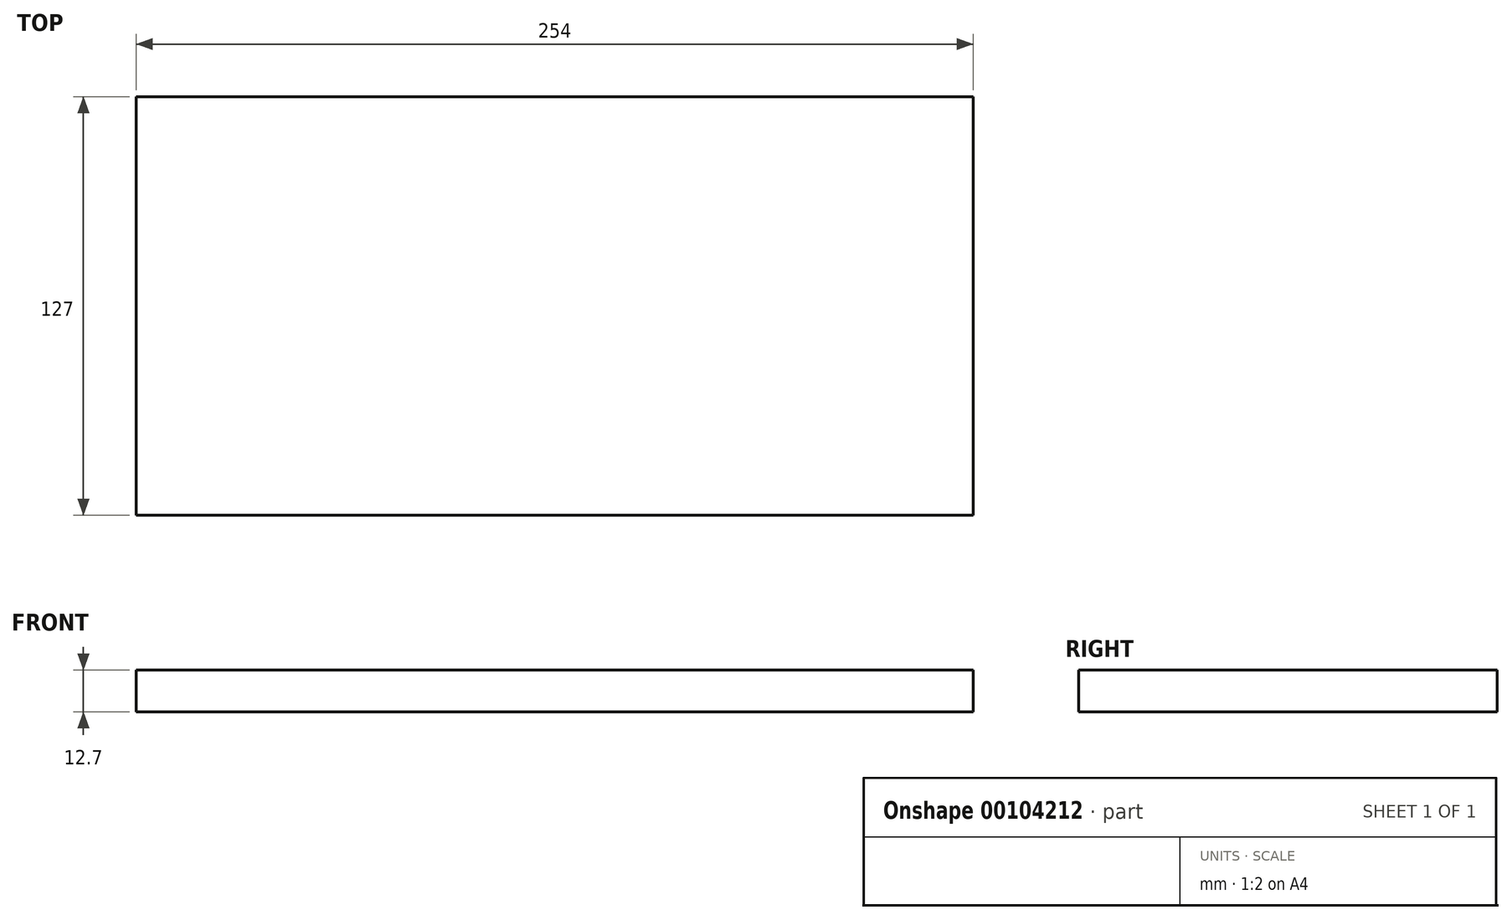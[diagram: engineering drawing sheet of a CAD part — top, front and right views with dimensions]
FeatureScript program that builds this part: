
annotation { "Feature Type Name" : "Feature", "Feature Type Description" : "" }
export const myFeature = defineFeature(function(context is Context, id is Id, definition is map)
    precondition{}
    {
        {
            var Q0;
            Q0=qCreatedBy(makeId("Top.planeOp"),FACE);
            var sketch = newSketch(context, id + "F0", { "sketchPlane" : qUnion([Q0])});
            skLineSegment(sketch, "E0.bottom", {"start": v(-114.28, -38.03) * mm, "end": v(139.72, -38.03) * mm});
            skLineSegment(sketch, "E0.top", {"start": v(-114.28, -165.03) * mm, "end": v(139.72, -165.03) * mm});
            skLineSegment(sketch, "E0.left", {"start": v(-114.28, -38.03) * mm, "end": v(-114.28, -165.03) * mm});
            skLineSegment(sketch, "E0.right", {"start": v(139.72, -38.03) * mm, "end": v(139.72, -165.03) * mm});
            skSolve(sketch);
        }
        {
            var Q0;
            Q0=makeQuery(id+"F0.imprint","IMPRINT",FACE,{"disambiguationData":[TD([[makeQuery(id+"F0.imprint","IMPRINT",EDGE,{"derivedFrom":sQuery(id+"F0.wireOp",EDGE,"E0.bottom")}),-1.0]])]});
            extrude(context, id + "F1", {"entities" : qUnion([Q0]), "oppositeDirection" : true, "depth" : 12.7 * mm});
        }
    });
